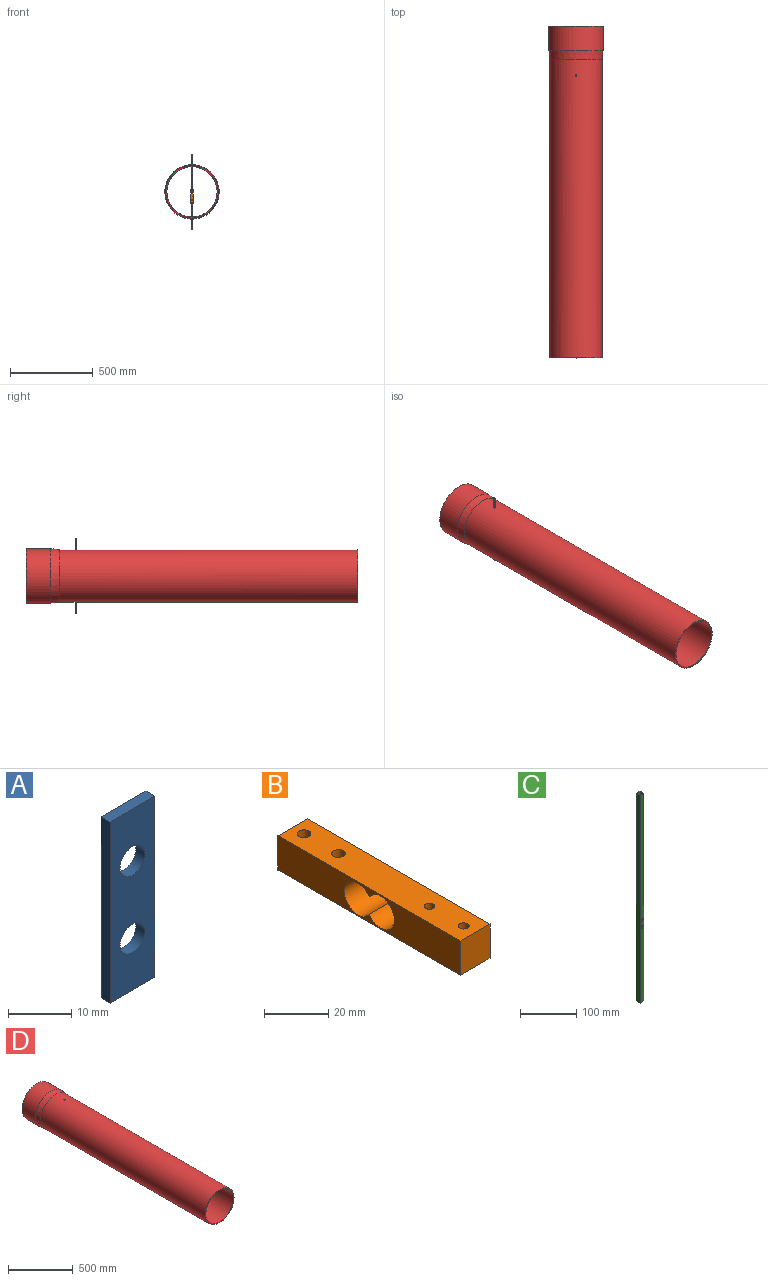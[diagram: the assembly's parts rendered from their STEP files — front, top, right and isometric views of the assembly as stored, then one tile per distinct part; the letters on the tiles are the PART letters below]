
ASSEMBLY  parts=4 mates=3
PART A: 8 faces, bbox 10x2x35 mm
  f0: plane 35x2mm, normal (-1,0,0), area 70mm2, adj f1,f3,f4,f5
  f1: plane 10x2mm, normal (0,0,-1), area 20mm2, adj f0,f2,f4,f5
  f2: plane 35x2mm, normal (1,0,0), area 70mm2, adj f1,f3,f4,f5
  f3: plane 10x2mm, normal (0,0,1), area 20mm2, adj f0,f2,f4,f5
  f4: plane 35x10mm, normal (0,-1,0), area 302.5mm2, adj f0,f1,f2,f3,f6,f7
  f5: plane 35x10mm, normal (0,1,0), area 302.5mm2, adj f0,f1,f2,f3,f6,f7
  f6: cylinder r=2.75mm len=5.5mm, axis (0,1,0), area 34.6mm2, adj f4,f5
  f7: cylinder r=2.75mm len=5.5mm, axis (0,1,0), area 34.6mm2, adj f4,f5
PART B: 12 faces, bbox 13x80x13 mm
  f0: plane 80x13mm, normal (1,0,0), area 822.8mm2, adj f2,f3,f4,f5,f6,f7
  f1: plane 80x13mm, normal (-1,0,0), area 822.8mm2, adj f2,f3,f4,f5,f6,f7
  f2: plane 80x13mm, normal (0,0,1), area 995.2mm2, adj f0,f1,f4,f5,f8,f9,f10,f11
  f3: plane 80x13mm, normal (0,0,-1), area 995.2mm2, adj f0,f1,f4,f5,f8,f9,f10,f11
  f4: plane 13x13mm, normal (0,-1,0), area 169mm2, adj f0,f1,f2,f3
  f5: plane 13x13mm, normal (0,1,0), area 169mm2, adj f0,f1,f2,f3
  f6: cylinder r=6mm len=13mm, axis (-1,0,0), area 398.7mm2, adj f0,f1,f7
  f7: cylinder r=6mm len=13mm, axis (-1,0,0), area 398.7mm2, adj f0,f1,f6
  f8: cylinder r=1.65mm len=13mm, axis (0,0,1), area 134.8mm2, adj f2,f3
  f9: cylinder r=1.65mm len=13mm, axis (0,0,1), area 134.8mm2, adj f2,f3
  f10: cylinder r=2.1mm len=13mm, axis (0,0,1), area 171.5mm2, adj f2,f3
  f11: cylinder r=2.1mm len=13mm, axis (0,0,1), area 171.5mm2, adj f2,f3
PART C: 14 faces, bbox 10x10x450 mm
  f0: plane 10x10mm, normal (0,0,1), area 36mm2, adj f2,f3,f4,f5,f6,f7,f8,f9
  f1: plane 10x10mm, normal (0,0,-1), area 36mm2, adj f2,f3,f4,f5,f6,f7,f8,f9
  f2: plane 450x10mm, normal (0,-1,0), area 4452.5mm2, adj f0,f1,f3,f5,f11,f13
  f3: plane 450x10mm, normal (1,0,0), area 4500mm2, adj f0,f1,f2,f4
  f4: plane 450x10mm, normal (0,1,0), area 4452.5mm2, adj f0,f1,f3,f5,f10,f12
  f5: plane 450x10mm, normal (-1,0,0), area 4500mm2, adj f0,f1,f2,f4
  f6: plane 450x8mm, normal (0,1,0), area 3552.5mm2, adj f0,f1,f7,f9,f11,f13
  f7: plane 450x8mm, normal (-1,0,0), area 3600mm2, adj f0,f1,f6,f8
  f8: plane 450x8mm, normal (0,-1,0), area 3552.5mm2, adj f0,f1,f7,f9,f10,f12
  f9: plane 450x8mm, normal (1,0,0), area 3600mm2, adj f0,f1,f6,f8
  f10: cylinder r=2.75mm len=5.5mm, axis (0,-1,0), area 17.3mm2, adj f4,f8
  f11: cylinder r=2.75mm len=5.5mm, axis (0,-1,0), area 17.3mm2, adj f2,f6
  f12: cylinder r=2.75mm len=5.5mm, axis (0,-1,0), area 17.3mm2, adj f4,f8
  f13: cylinder r=2.75mm len=5.5mm, axis (0,-1,0), area 17.3mm2, adj f2,f6
PART D: 16 faces, bbox 327.4x2000x327.4 mm
  f0: cylinder r=157.5mm len=1800mm, axis (0,1,0), area 1781083mm2, adj f2,f3,f8,f9,f10,f11,f12,f13
  f1: cylinder r=151.3mm len=1800.38mm, axis (0,1,0), area 1711326.7mm2, adj f2,f6,f8,f9,f10,f11,f12,f13
  f2: plane 315x315mm, normal (0,-1,0), area 6014.8mm2, adj f0,f1
  f3: cone r=163.7mm half-angle=7.1deg, axis (0,1,0), area 50840.4mm2, adj f0,f4
  f4: cylinder r=163.7mm len=327.4mm, axis (0,-1,0), area 154283.6mm2, adj f3,f5
  f5: plane 327.4x327.4mm, normal (0,1,0), area 6256.3mm2, adj f4,f7
  f6: cone r=157.55mm half-angle=7.1deg, axis (0,1,0), area 48877.7mm2, adj f1,f7
  f7: cylinder r=157.5mm len=315mm, axis (0,-1,0), area 148061.3mm2, adj f5,f6
  f8: plane 10x6.2mm, normal (1,0,0), area 62mm2, adj f0,f1,f9,f11
  f9: plane 10x6.28mm, normal (0,-1,0), area 62mm2, adj f0,f1,f8,f10
  f10: plane 10x6.2mm, normal (-1,0,0), area 62mm2, adj f0,f1,f9,f11
  f11: plane 10x6.28mm, normal (0,1,0), area 62mm2, adj f0,f1,f8,f10
  f12: plane 10x6.28mm, normal (0,1,0), area 62mm2, adj f0,f1,f13,f15
  f13: plane 10x6.2mm, normal (-1,0,0), area 62mm2, adj f0,f1,f12,f14
  f14: plane 10x6.28mm, normal (0,-1,0), area 62mm2, adj f0,f1,f13,f15
  f15: plane 10x6.2mm, normal (1,0,0), area 62mm2, adj f0,f1,f12,f14
PLACE A rot(axis=(0,1,0),180deg) t=(844.62,1514.22,415.29)mm
PLACE B rot(axis=(-1,0,0),90deg) t=(844.62,1400.72,497.79)mm
PLACE C t=(844.62,1514.22,525.29)mm
PLACE D t=(844.62,1514.22,525.88)mm
MATE fastened B.f10 <-> A.f7  axis (0,1,0) through (844.62,1407.22,477.79)mm
MATE fastened A.f6 <-> C.f12  axis (0,1,0) through (844.62,1409.22,462.79)mm
MATE fastened D.f0 <-> C.f2  axis (0,1,0) through (844.62,1409.22,525.88)mm
